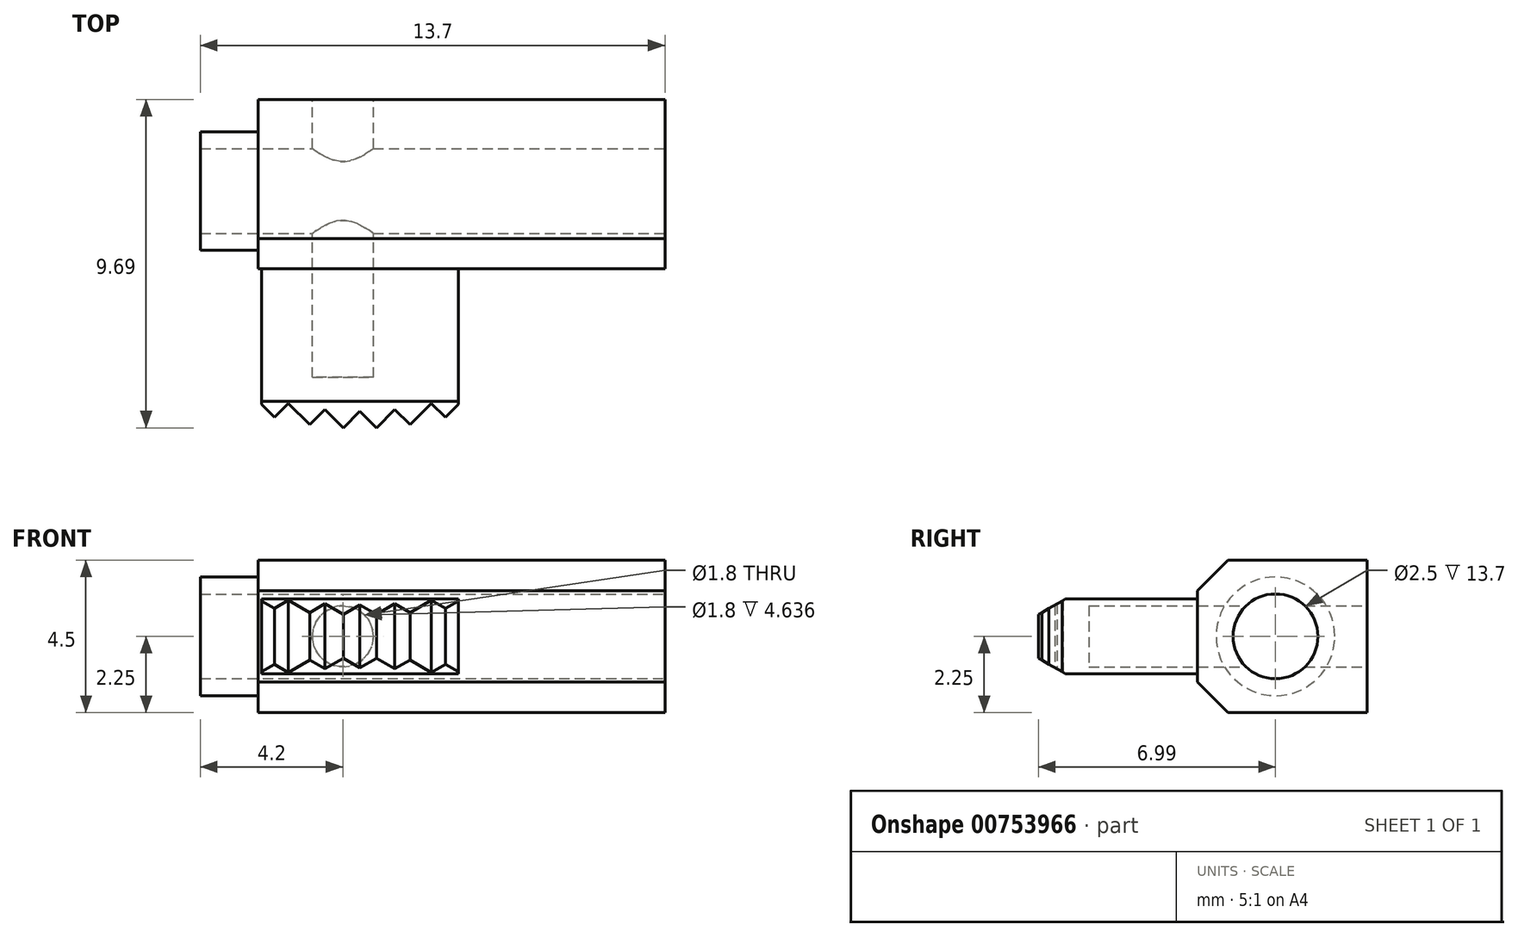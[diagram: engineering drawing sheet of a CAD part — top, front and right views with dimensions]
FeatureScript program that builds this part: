
annotation { "Feature Type Name" : "Feature", "Feature Type Description" : "" }
export const myFeature = defineFeature(function(context is Context, id is Id, definition is map)
    precondition{}
    {
        {
            var Q0;
            Q0=qCreatedBy(makeId("Top.planeOp"),FACE);
            var sketch = newSketch(context, id + "F0", { "sketchPlane" : qUnion([Q0])});
            skLineSegment(sketch, "E0", {"start": v(0, 5) * mm, "end": v(0, 0) * mm});
            skLineSegment(sketch, "E1", {"start": v(0, 0) * mm, "end": v(-12, 0) * mm});
            skLineSegment(sketch, "E2", {"start": v(-12, 0) * mm, "end": v(-12, 5) * mm});
            skLineSegment(sketch, "E3", {"start": v(-12, 5) * mm, "end": v(0, 5) * mm});
            skLineSegment(sketch, "E4.bottom", {"start": v(-11.9, 0) * mm, "end": v(-6.1, 0) * mm});
            skLineSegment(sketch, "E4.top", {"start": v(-11.9, -4) * mm, "end": v(-6.1, -4) * mm, "construction": true});
            skLineSegment(sketch, "E4.left", {"start": v(-11.9, 0) * mm, "end": v(-11.9, -4) * mm});
            skLineSegment(sketch, "E4.right", {"start": v(-6.1, 0) * mm, "end": v(-6.1, -4) * mm});
            skPoint(sketch, "E5", {"position": v(-9, -4) * mm});
            skCircle(sketch, "E6", {"center": v(-9, 5.3) * mm, "radius": 10 * mm, "construction": true});
            skCircle(sketch, "E7", {"center": v(-9, 5.3) * mm, "radius": 9.5 * mm, "construction": true});
            skLineSegment(sketch, "E8", {"start": v(-9, 5.3) * mm, "end": v(-9, -4.7) * mm, "construction": true});
            skLineSegment(sketch, "E9", {"start": v(-9, -4.2) * mm, "end": v(-9.49, -4.69) * mm});
            skLineSegment(sketch, "E10", {"start": v(-9, -4.2) * mm, "end": v(-8.51, -4.69) * mm});
            skLineSegment(sketch, "E11", {"start": v(-9.49, -4.69) * mm, "end": v(-10.03, -4.14) * mm});
            skLineSegment(sketch, "E12", {"start": v(-10.03, -4.14) * mm, "end": v(-10.48, -4.6) * mm});
            skLineSegment(sketch, "E13", {"start": v(-10.48, -4.6) * mm, "end": v(-11.1, -3.96) * mm});
            skLineSegment(sketch, "E14", {"start": v(-11.1, -3.96) * mm, "end": v(-11.52, -4.38) * mm});
            skLineSegment(sketch, "E15", {"start": v(-11.52, -4.38) * mm, "end": v(-11.9, -4) * mm});
            skLineSegment(sketch, "E16", {"start": v(-8.51, -4.69) * mm, "end": v(-7.97, -4.14) * mm});
            skLineSegment(sketch, "E17", {"start": v(-7.97, -4.14) * mm, "end": v(-7.52, -4.6) * mm});
            skLineSegment(sketch, "E18", {"start": v(-7.52, -4.6) * mm, "end": v(-6.9, -3.96) * mm});
            skLineSegment(sketch, "E19", {"start": v(-6.9, -3.96) * mm, "end": v(-6.48, -4.38) * mm});
            skLineSegment(sketch, "E20", {"start": v(-6.48, -4.38) * mm, "end": v(-6.1, -4) * mm});
            skSolve(sketch);
        }
        {
            var Q0;
            {var subQ4=sQuery(id+"F0.wireOp",EDGE,"E0");Q0=makeQuery(id+"F0.imprint","IMPRINT",FACE,{"disambiguationData":[TD([[makeQuery(id+"F0.imprint","IMPRINT",EDGE,{"derivedFrom":subQ4}),-1.0]])]});}
            extrude(context, id + "F1", {"entities" : qUnion([Q0]), "endBound" : BoundingType.SYMMETRIC, "depth" : 4.5 * mm});
        }
        {
            var Q0;
            {var subQ0=sQuery(id+"F0.wireOp",EDGE,"E4.left");Q0=makeQuery(id+"F0.imprint","IMPRINT",FACE,{"disambiguationData":[TD([[makeQuery(id+"F0.imprint","IMPRINT",EDGE,{"derivedFrom":subQ0}),1.0]])]});}
            extrude(context, id + "F2", {"entities" : qUnion([Q0]), "operationType" : NewBodyOperationType.ADD, "endBound" : BoundingType.SYMMETRIC, "depth" : 2.2 * mm});
        }
        {
            var Q0;
            Q0=makeQuery(id+"F1.opExtrude","CAP_EDGE",EDGE,{"disambiguationData":[OSD([sQuery(id+"F0.wireOp",EDGE,"E1")])],"isStart":false});
            var Q1;
            Q1=makeQuery(id+"F1.opExtrude","CAP_EDGE",EDGE,{"disambiguationData":[OSD([sQuery(id+"F0.wireOp",EDGE,"E1")])],"isStart":true});
            chamfer(context, id + "F3", {"entities" : qUnion([Q0, Q1]), "width" : 0.9 * mm, "tangentPropagation" : true});
        }
        {
            var Q0;
            Q0=qCreatedBy(makeId("Right.planeOp"),FACE);
            var sketch = newSketch(context, id + "F4", { "sketchPlane" : qUnion([Q0])});
            skLineSegment(sketch, "E21", {"start": v(-3.9, -1.1) * mm, "end": v(-3.9, 1.1) * mm});
            skLineSegment(sketch, "E22", {"start": v(-3.9, 1.1) * mm, "end": v(-4.9, 0.52) * mm});
            skLineSegment(sketch, "E23", {"start": v(-4.9, 0.52) * mm, "end": v(-4.9, -0.52) * mm});
            skLineSegment(sketch, "E24", {"start": v(-4.9, -0.52) * mm, "end": v(-3.9, -1.1) * mm});
            skLineSegment(sketch, "E25", {"start": v(-3.9, 1.1) * mm, "end": v(-4.9, 1.1) * mm});
            skLineSegment(sketch, "E26", {"start": v(-4.9, 1.1) * mm, "end": v(-4.9, -1.1) * mm});
            skLineSegment(sketch, "E27", {"start": v(-4.9, -1.1) * mm, "end": v(-3.9, -1.1) * mm});
            skSolve(sketch);
        }
        {
            var Q0;
            {var subQ0=sQuery(id+"F4.wireOp",EDGE,"E22");Q0=makeQuery(id+"F4.imprint","IMPRINT",FACE,{"disambiguationData":[TD([[makeQuery(id+"F4.imprint","IMPRINT",EDGE,{"derivedFrom":subQ0}),-1.0]])]});}
            var Q1;
            {var subQ0=sQuery(id+"F4.wireOp",EDGE,"E24");Q1=makeQuery(id+"F4.imprint","IMPRINT",FACE,{"disambiguationData":[TD([[makeQuery(id+"F4.imprint","IMPRINT",EDGE,{"derivedFrom":subQ0}),-1.0]])]});}
            extrude(context, id + "F5", {"entities" : qUnion([Q0, Q1]), "operationType" : NewBodyOperationType.REMOVE, "oppositeDirection" : true, "depth" : 12 * mm});
        }
        {
            var Q0;
            Q0=makeQuery(id+"F1.opExtrude","SWEPT_FACE",FACE,{"disambiguationData":[OSD([sQuery(id+"F0.wireOp",EDGE,"E2")])]});
            var sketch = newSketch(context, id + "F6", { "sketchPlane" : qUnion([Q0])});
            skCircle(sketch, "E28", {"center": v(-2.3, 0) * mm, "radius": 1.25 * mm});
            skCircle(sketch, "E29", {"center": v(-2.3, 0) * mm, "radius": 1.75 * mm});
            skSolve(sketch);
        }
        {
            var Q0;
            Q0=makeQuery(id+"F6.imprint","IMPRINT",FACE,{"disambiguationData":[TD([[makeQuery(id+"F6.imprint","IMPRINT",EDGE,{"derivedFrom":sQuery(id+"F6.wireOp",EDGE,"E28")}),-1.0]])]});
            extrude(context, id + "F7", {"entities" : qUnion([Q0]), "operationType" : NewBodyOperationType.ADD, "depth" : 1.7 * mm});
        }
        {
            var Q0;
            Q0=makeQuery(id+"F6.imprint","IMPRINT",FACE,{"disambiguationData":[TD([[makeQuery(id+"F6.imprint","IMPRINT",EDGE,{"derivedFrom":sQuery(id+"F6.wireOp",EDGE,"E28")}),1.0]])]});
            extrude(context, id + "F8", {"entities" : qUnion([Q0]), "operationType" : NewBodyOperationType.REMOVE, "endBound" : BoundingType.THROUGH_ALL, "oppositeDirection" : true, "depth" : 25 * mm});
        }
        {
            var Q0;
            Q0=makeQuery(id+"F1.opExtrude","SWEPT_FACE",FACE,{"disambiguationData":[OSD([sQuery(id+"F0.wireOp",EDGE,"E3")])]});
            var sketch = newSketch(context, id + "F9", { "sketchPlane" : qUnion([Q0])});
            skCircle(sketch, "E30", {"center": v(9.5, 0) * mm, "radius": 0.9 * mm});
            skSolve(sketch);
        }
        {
            var Q0;
            Q0=makeQuery(id+"F9.imprint","IMPRINT",FACE,{"disambiguationData":[TD([[makeQuery(id+"F9.imprint","IMPRINT",EDGE,{"derivedFrom":sQuery(id+"F9.wireOp",EDGE,"E30")}),1.0]])]});
            extrude(context, id + "F10", {"entities" : qUnion([Q0]), "operationType" : NewBodyOperationType.REMOVE, "oppositeDirection" : true, "depth" : 8.2 * mm});
        }
    });
